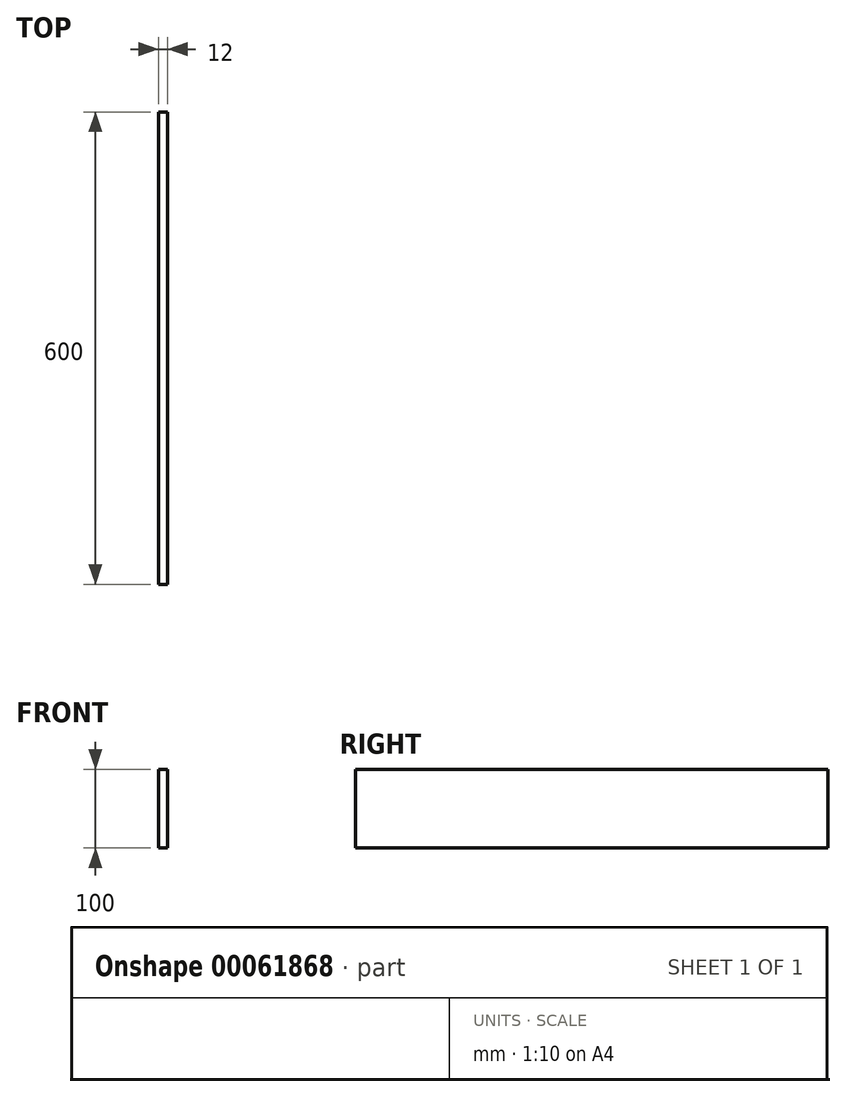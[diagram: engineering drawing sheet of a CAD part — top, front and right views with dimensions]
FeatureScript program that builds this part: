
annotation { "Feature Type Name" : "Feature", "Feature Type Description" : "" }
export const myFeature = defineFeature(function(context is Context, id is Id, definition is map)
    precondition{}
    {
        {
            var Q0;
            Q0=qCreatedBy(makeId("Right.planeOp"),FACE);
            var sketch = newSketch(context, id + "F0", { "sketchPlane" : qUnion([Q0])});
            skLineSegment(sketch, "E0.bottom", {"start": v(0, 0) * mm, "end": v(600, 0) * mm});
            skLineSegment(sketch, "E0.top", {"start": v(0, -100) * mm, "end": v(600, -100) * mm});
            skLineSegment(sketch, "E0.left", {"start": v(0, 0) * mm, "end": v(0, -100) * mm});
            skLineSegment(sketch, "E0.right", {"start": v(600, 0) * mm, "end": v(600, -100) * mm});
            skSolve(sketch);
        }
        {
            var Q0;
            Q0=makeQuery(id+"F0.imprint","IMPRINT",FACE,{"disambiguationData":[TD([[makeQuery(id+"F0.imprint","IMPRINT",EDGE,{"derivedFrom":sQuery(id+"F0.wireOp",EDGE,"E0.bottom")}),-1.0]])]});
            extrude(context, id + "F1", {"entities" : qUnion([Q0]), "depth" : 12 * mm});
        }
    });
